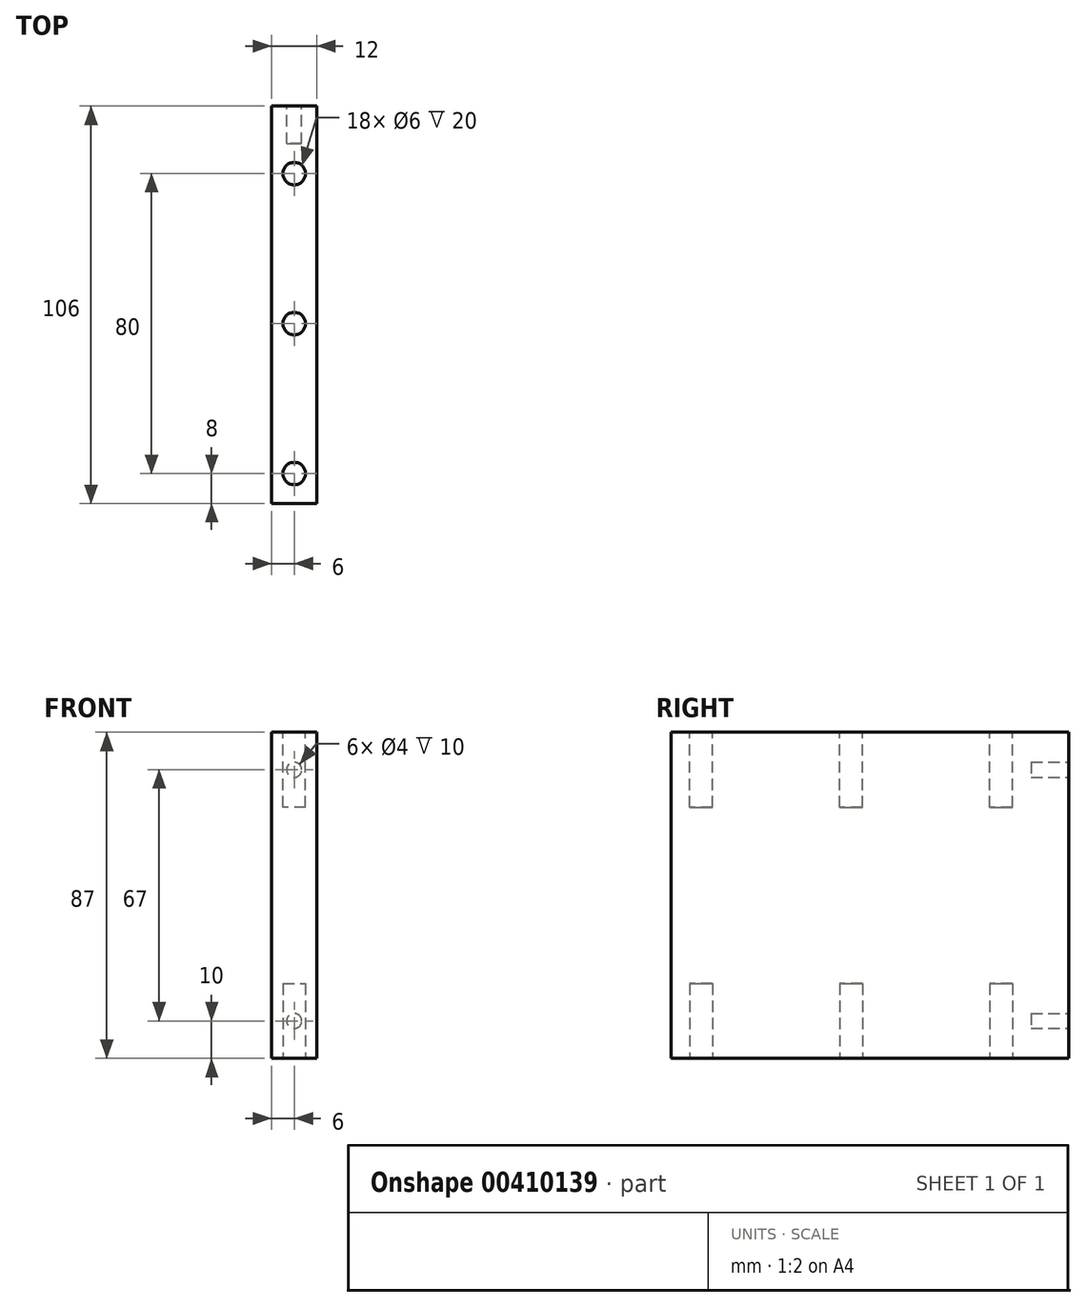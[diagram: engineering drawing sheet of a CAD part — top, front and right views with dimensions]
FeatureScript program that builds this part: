
annotation { "Feature Type Name" : "Feature", "Feature Type Description" : "" }
export const myFeature = defineFeature(function(context is Context, id is Id, definition is map)
    precondition{}
    {
        {
            var Q0;
            Q0=qCreatedBy(makeId("Right.planeOp"),FACE);
            var sketch = newSketch(context, id + "F0", { "sketchPlane" : qUnion([Q0])});
            skLineSegment(sketch, "E0.bottom", {"start": v(0, 0) * mm, "end": v(106, 0) * mm});
            skLineSegment(sketch, "E0.top", {"start": v(0, 87) * mm, "end": v(106, 87) * mm});
            skLineSegment(sketch, "E0.left", {"start": v(0, 0) * mm, "end": v(0, 87) * mm});
            skLineSegment(sketch, "E0.right", {"start": v(106, 0) * mm, "end": v(106, 87) * mm});
            skPoint(sketch, "E1", {"position": v(0, 43.5) * mm});
            skPoint(sketch, "E2", {"position": v(106, 43.5) * mm});
            skSolve(sketch);
        }
        {
            var Q0;
            Q0=qSketchRegion(id+"F0",true);
            extrude(context, id + "F1", {"entities" : qUnion([Q0]), "depth" : 12 * mm});
        }
        {
            var Q0;
            Q0=makeQuery(id+"F1.opExtrude","SWEPT_FACE",FACE,{"disambiguationData":[OSD([sQuery(id+"F0.wireOp",EDGE,"E0.top")])]});
            var sketch = newSketch(context, id + "F2", { "sketchPlane" : qUnion([Q0])});
            skLineSegment(sketch, "E3", {"start": v(6, 106) * mm, "end": v(6, 0) * mm, "construction": true});
            skCircle(sketch, "E4", {"center": v(6, 88) * mm, "radius": 3 * mm});
            skCircle(sketch, "E5.0.1.0", {"center": v(6, 48) * mm, "radius": 3 * mm});
            skCircle(sketch, "E5.0.2.0", {"center": v(6, 8) * mm, "radius": 3 * mm});
            skLineSegment(sketch, "E5.direction1", {"start": v(6, 88) * mm, "end": v(31, 88) * mm, "construction": true});
            skLineSegment(sketch, "E5.direction2", {"start": v(6, 88) * mm, "end": v(6, 48) * mm, "construction": true});
            skSolve(sketch);
        }
        {
            var Q0;
            Q0 = qSketchRegion(id + "F2", true);
            extrude(context, id + "F3", {"entities" : qUnion([Q0]), "operationType" : NewBodyOperationType.REMOVE, "oppositeDirection" : true, "depth" : 20 * mm});
        }
        {
            var Q0;
            Q0=makeQuery(id+"F1.opExtrude","SWEPT_FACE",FACE,{"disambiguationData":[OSD([sQuery(id+"F0.wireOp",EDGE,"E0.bottom")])]});
            var sketch = newSketch(context, id + "F4", { "sketchPlane" : qUnion([Q0])});
            skLineSegment(sketch, "E6.0", {"start": v(6, -106) * mm, "end": v(6, 0) * mm});
            skCircle(sketch, "E6.1", {"center": v(6, -88) * mm, "radius": 3 * mm});
            skCircle(sketch, "E6.2", {"center": v(6, -48) * mm, "radius": 3 * mm});
            skCircle(sketch, "E6.3", {"center": v(6, -8) * mm, "radius": 3 * mm});
            skLineSegment(sketch, "E6.4", {"start": v(6, -88) * mm, "end": v(31, -88) * mm});
            skLineSegment(sketch, "E6.5", {"start": v(6, -88) * mm, "end": v(6, -48) * mm});
            skSolve(sketch);
        }
        {
            var Q0;
            Q0 = qSketchRegion(id + "F2", true);
            extrude(context, id + "F5", {"entities" : qUnion([Q0]), "operationType" : NewBodyOperationType.REMOVE, "oppositeDirection" : true, "depth" : 20 * mm});
        }
        {
            var Q0;
            Q0 = qSketchRegion(id + "F4", true);
            extrude(context, id + "F6", {"entities" : qUnion([Q0]), "operationType" : NewBodyOperationType.REMOVE, "oppositeDirection" : true, "depth" : 20 * mm});
        }
        {
            var Q0;
            Q0=makeQuery(id+"F1.opExtrude","SWEPT_FACE",FACE,{"disambiguationData":[OSD([sQuery(id+"F0.wireOp",EDGE,"E0.right")])]});
            var sketch = newSketch(context, id + "F7", { "sketchPlane" : qUnion([Q0])});
            skLineSegment(sketch, "E7", {"start": v(-6, 87) * mm, "end": v(-6, 0) * mm, "construction": true});
            skCircle(sketch, "E8", {"center": v(-6, 77) * mm, "radius": 2 * mm});
            skCircle(sketch, "E9", {"center": v(-6, 10) * mm, "radius": 2 * mm});
            skSolve(sketch);
        }
        {
            var Q0;
            Q0 = qSketchRegion(id + "F7", true);
            extrude(context, id + "F8", {"entities" : qUnion([Q0]), "operationType" : NewBodyOperationType.REMOVE, "oppositeDirection" : true, "depth" : 10 * mm});
        }
    });
